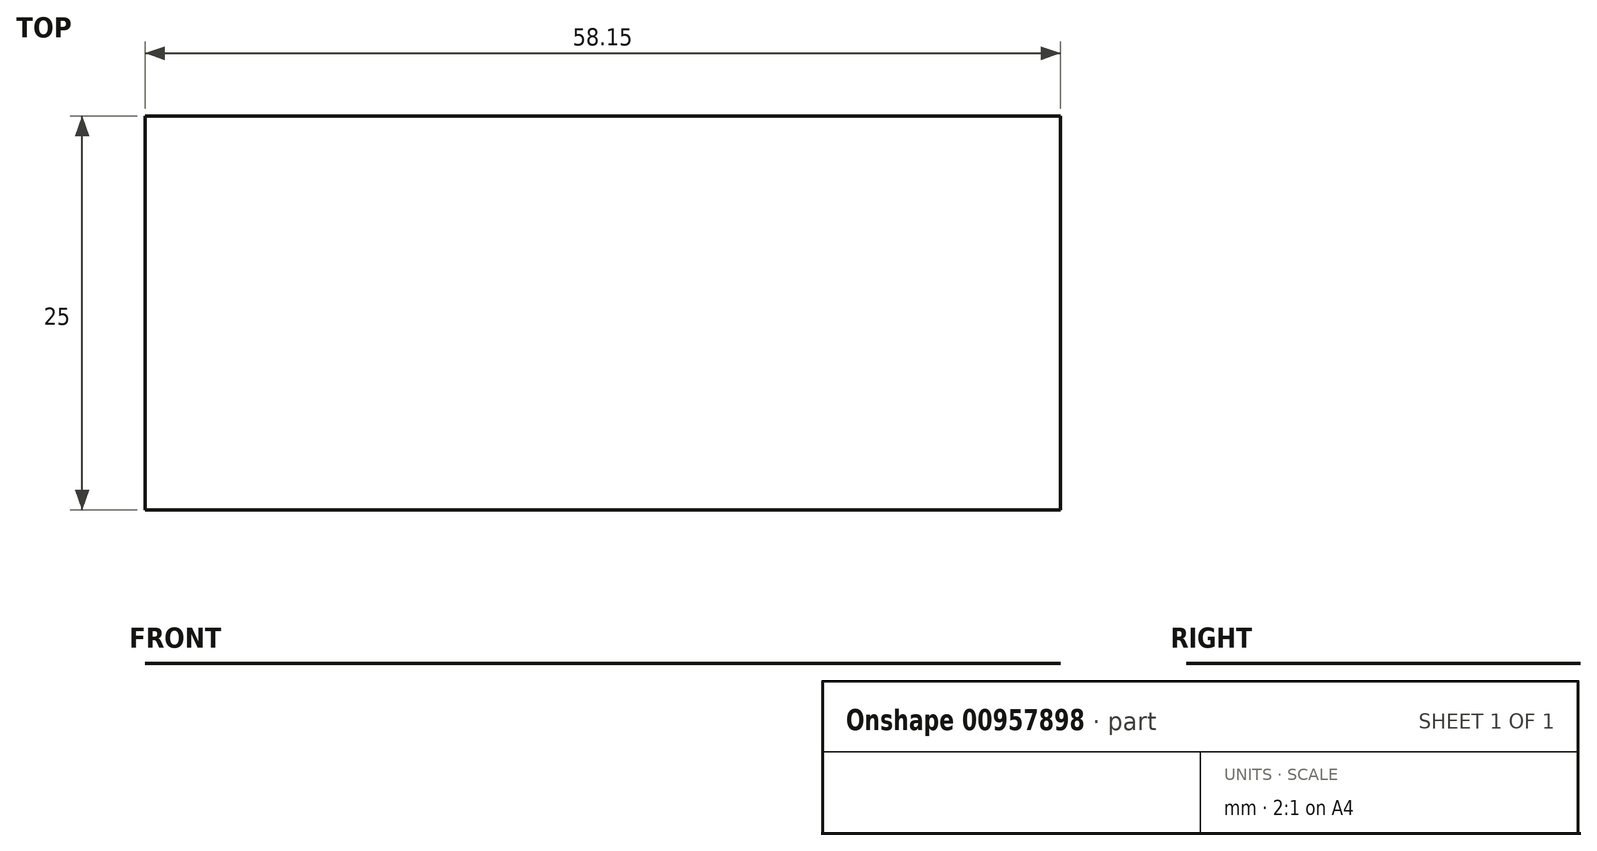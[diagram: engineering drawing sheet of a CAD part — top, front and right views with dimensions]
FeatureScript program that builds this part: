
annotation { "Feature Type Name" : "Feature", "Feature Type Description" : "" }
export const myFeature = defineFeature(function(context is Context, id is Id, definition is map)
    precondition{}
    {
        {
            var Q0;
            Q0=qCreatedBy(makeId("Front.planeOp"),FACE);
            var sketch = newSketch(context, id + "F0", { "sketchPlane" : qUnion([Q0])});
            skLineSegment(sketch, "E0.bottom", {"start": v(-24.17, 44.26) * mm, "end": v(33.98, 44.26) * mm});
            skLineSegment(sketch, "E0.top", {"start": v(-24.17, -41.88) * mm, "end": v(33.98, -41.88) * mm});
            skLineSegment(sketch, "E0.left", {"start": v(-24.17, 44.26) * mm, "end": v(-24.17, -41.88) * mm});
            skLineSegment(sketch, "E0.right", {"start": v(33.98, 44.26) * mm, "end": v(33.98, -41.88) * mm});
            skSolve(sketch);
        }
        {
            var Q0;
            Q0=sQuery(id+"F0.wireOp",EDGE,"E0.bottom");
            extrude(context, id + "F1", {"bodyType" : ToolBodyType.SURFACE, "surfaceEntities" : qUnion([Q0]), "depth" : 25 * mm, "offsetDistance" : 25 * mm});
        }
    });
